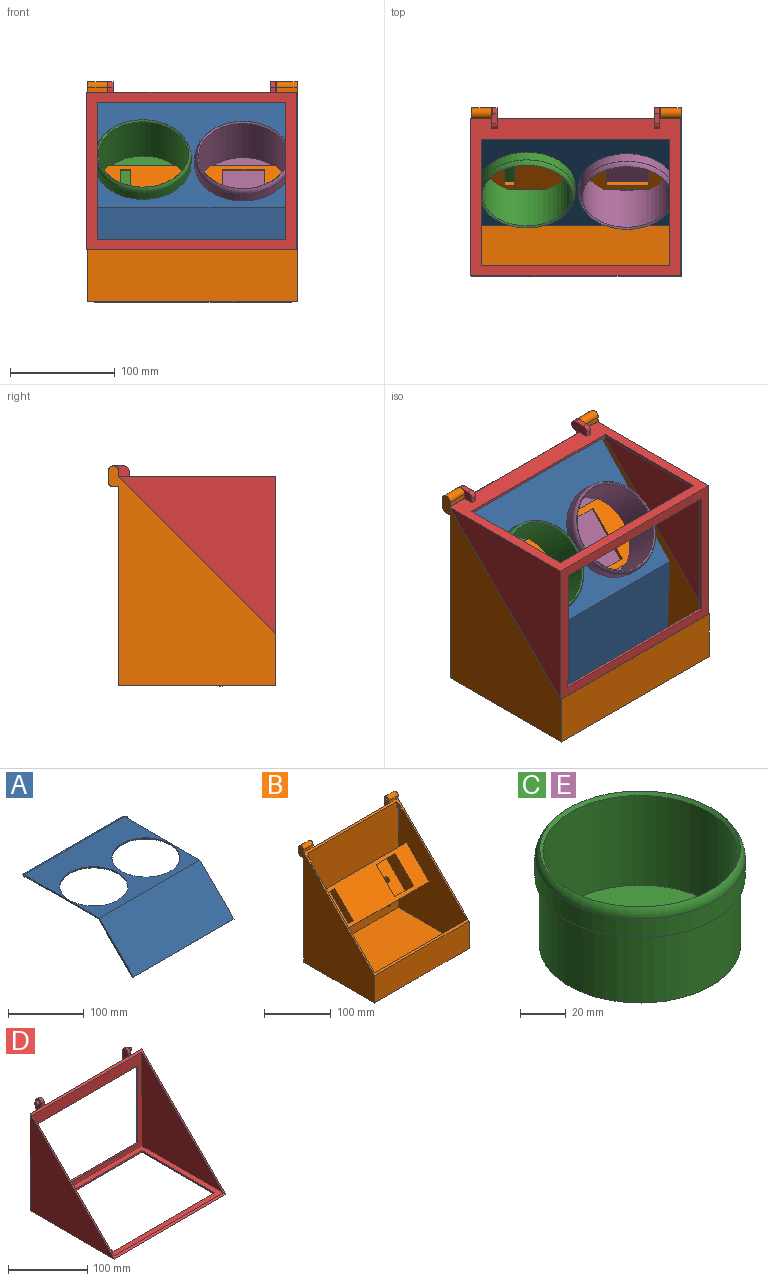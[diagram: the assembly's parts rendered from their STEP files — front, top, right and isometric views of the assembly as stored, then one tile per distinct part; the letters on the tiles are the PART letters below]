
ASSEMBLY  parts=5 mates=4
PART A: 18 faces, bbox 192x208.6x65.6 mm
  f0: plane 4.88x2mm, normal (-1,0,0), area 6.8mm2, adj f4,f5,f8,f13
  f1: plane 4.88x2mm, normal (1,0,0), area 6.8mm2, adj f4,f5,f8,f10
  f2: plane 201.52x65.64mm, normal (-1,0,0), area 527.8mm2, adj f4,f5,f12,f15,f16,f17
  f3: plane 201.52x65.64mm, normal (1,0,0), area 527.8mm2, adj f4,f5,f9,f15,f16,f17
  f4: plane 192x141mm, normal (0,0,1), area 13793.5mm2, adj f0,f1,f2,f3,f6,f7,f8,f9
  f5: plane 192x143mm, normal (0,0,-1), area 14169.5mm2, adj f0,f1,f2,f3,f6,f7,f8,f9
  f6: cylinder r=45mm len=90mm, axis (0,0,1), area 565.5mm2, adj f4,f5
  f7: cylinder r=45mm len=90mm, axis (0,0,1), area 565.5mm2, adj f4,f5
  f8: cylinder r=5mm len=188mm, axis (1,0,0), area 871.7mm2, adj f0,f1,f4,f5
  f9: cylinder r=1.5mm len=2mm, axis (-1,0,0), area 4.4mm2, adj f3,f4,f5,f11
  f10: cylinder r=1.5mm len=2mm, axis (-1,0,0), area 4.4mm2, adj f1,f4,f5,f11
  f11: plane 3x2mm, normal (1,0,0), area 5.5mm2, adj f4,f5,f9,f10
  f12: cylinder r=1.5mm len=2mm, axis (1,0,0), area 4.4mm2, adj f2,f4,f5,f14
  f13: cylinder r=1.5mm len=2mm, axis (1,0,0), area 4.4mm2, adj f0,f4,f5,f14
  f14: plane 3x2mm, normal (-1,0,0), area 5.5mm2, adj f4,f5,f12,f13
  f15: plane 188x63.64mm, normal (0,0.71,-0.71), area 16920mm2, adj f2,f3,f5,f17
  f16: plane 188x63.64mm, normal (0,-0.71,0.71), area 16920mm2, adj f2,f3,f4,f17
  f17: plane 188x2mm, normal (0,-0.71,-0.71), area 531.7mm2, adj f2,f3,f15,f16
PART B: 60 faces, bbox 200x160x210 mm
  f0: plane 19.69x19.58mm, normal (0,-0.71,0.71), area 238.4mm2, adj f43,f44,f45,f56
  f1: plane 185x145mm, normal (-1,0,0), area 14879.1mm2, adj f2,f4,f5,f11,f12,f32,f42,f49
  f2: plane 195x84.64mm, normal (0,-1,0), area 16445.5mm2, adj f1,f3,f4,f30,f31,f32,f33,f49
  f3: plane 185x145mm, normal (1,0,0), area 14879.1mm2, adj f2,f4,f5,f11,f12,f30,f42,f49
  f4: plane 200x150mm, normal (0,-0.71,0.71), area 2495.2mm2, adj f1,f2,f3,f6,f7,f8,f9,f11
  f5: plane 195x62.42mm, normal (0,-1,0), area 12093.3mm2, adj f1,f3,f12,f29,f42
  f6: plane 200x200mm, normal (0,1,0), area 39521.5mm2, adj f4,f7,f9,f10,f13,f14,f16,f17
  f7: plane 210x160mm, normal (-1,0,0), area 18933.9mm2, adj f4,f6,f8,f10,f16,f18,f20,f26
  f8: plane 200x50mm, normal (0,-1,0), area 10000mm2, adj f4,f7,f9,f10
  f9: plane 210x160mm, normal (1,0,0), area 18933.9mm2, adj f4,f6,f8,f10,f13,f15,f19,f25
  f10: plane 200x150mm, normal (0,0,-1), area 30000mm2, adj f6,f7,f8,f9
  f11: plane 195x50mm, normal (0,1,0), area 9750mm2, adj f1,f3,f4,f12
  f12: plane 195x145mm, normal (0,0,1), area 28275mm2, adj f1,f3,f5,f11
  f13: plane 20x5mm, normal (0,0,-1), area 100mm2, adj f6,f9,f14,f28
  f14: plane 20x10mm, normal (-1,0,0), area 164.3mm2, adj f6,f13,f15,f19,f22,f25,f28
  f15: plane 20x10mm, normal (0,1,0), area 200mm2, adj f9,f14,f25,f28
  f16: plane 20x5mm, normal (0,0,-1), area 100mm2, adj f6,f7,f17,f27
  f17: plane 20x10mm, normal (1,0,0), area 164.3mm2, adj f6,f16,f18,f20,f24,f26,f27
  f18: plane 20x10mm, normal (0,1,0), area 200mm2, adj f7,f17,f26,f27
  f19: plane 20x5mm, normal (0,-1,0), area 100mm2, adj f4,f9,f14,f25
  f20: plane 20x5mm, normal (0,-1,0), area 100mm2, adj f4,f7,f17,f26
  f21: cone r=0mm half-angle=59deg, axis (-1,0,0), area 22.9mm2, adj f22
  f22: cylinder r=2.5mm len=5mm, axis (-1,0,0), area 78.5mm2, adj f14,f21
  f23: cone r=0mm half-angle=59deg, axis (1,0,0), area 22.9mm2, adj f24
  f24: cylinder r=2.5mm len=5mm, axis (1,0,0), area 78.5mm2, adj f17,f23
  f25: cylinder r=5mm len=20mm, axis (1,0,0), area 314.2mm2, adj f9,f14,f15,f19
  f26: cylinder r=5mm len=20mm, axis (1,0,0), area 314.2mm2, adj f7,f17,f18,f20
  f27: cylinder r=5mm len=20mm, axis (1,0,0), area 157.1mm2, adj f7,f16,f17,f18
  f28: cylinder r=5mm len=20mm, axis (1,0,0), area 157.1mm2, adj f9,f13,f14,f15
  f29: cylinder r=5mm len=10mm, axis (0,1,0), area 78.5mm2, adj f5,f6
  f30: plane 10x3mm, normal (0,0,-1), area 30mm2, adj f2,f3,f4,f31
  f31: plane 10x10mm, normal (1,0,0), area 30mm2, adj f2,f4,f30,f34,f35,f36
  f32: plane 10x3mm, normal (0,0,-1), area 30mm2, adj f1,f2,f4,f33
  f33: plane 10x10mm, normal (-1,0,0), area 31.2mm2, adj f2,f4,f32,f38,f39,f40
  f34: plane 4.94x2mm, normal (0,0,1), area 9.9mm2, adj f31,f35,f36,f37
  f35: plane 6.74x2mm, normal (0,-1,0.08), area 13.5mm2, adj f4,f31,f34,f37
  f36: plane 2x1.42mm, normal (0,0.99,-0.12), area 2.9mm2, adj f4,f31,f34,f37
  f37: plane 6.74x5.49mm, normal (1,0,0), area 20mm2, adj f4,f34,f35,f36
  f38: plane 5x2mm, normal (0,0,1), area 10mm2, adj f33,f39,f40,f41
  f39: plane 2x1.25mm, normal (0,1,0), area 2.5mm2, adj f4,f33,f38,f41
  f40: plane 6.25x2mm, normal (0,-1,0), area 12.5mm2, adj f4,f33,f38,f41
  f41: plane 6.25x5mm, normal (-1,0,0), area 18.8mm2, adj f4,f38,f39,f40
  f42: plane 195x47.69mm, normal (0,0,-1), area 9298.8mm2, adj f1,f3,f5,f50
  f43: plane 57x56.89mm, normal (1,0,0), area 1388.3mm2, adj f0,f44,f52,f53,f55
  f44: plane 17.72x17.63mm, normal (0,-0.71,-0.71), area 250mm2, adj f0,f43,f45,f53
  f45: plane 57x56.89mm, normal (-1,0,0), area 1388.3mm2, adj f0,f44,f52,f53,f55
  f46: plane 40x17.72mm, normal (0,0.71,0.71), area 1000mm2, adj f47,f51,f53,f54
  f47: plane 57x56.89mm, normal (1,0,0), area 1388.3mm2, adj f46,f48,f53,f54
  f48: plane 40x17.72mm, normal (0,-0.71,-0.71), area 1000mm2, adj f47,f51,f53,f54
  f49: plane 195x17.72mm, normal (0,0.71,0.71), area 4875mm2, adj f1,f2,f3,f53
  f50: plane 195x17.72mm, normal (0,-0.71,-0.71), area 4875mm2, adj f1,f3,f42,f53
  f51: plane 57x56.89mm, normal (-1,0,0), area 1388.3mm2, adj f46,f48,f53,f54
  f52: plane 17.72x17.63mm, normal (0,0.71,0.71), area 250mm2, adj f43,f45,f53,f55
  f53: plane 195x47.94mm, normal (0,-0.71,0.71), area 10408.5mm2, adj f1,f3,f43,f44,f45,f46,f47,f48
  f54: plane 40x39.37mm, normal (0,-0.71,0.71), area 2142.8mm2, adj f46,f47,f48,f51,f58
  f55: plane 19.69x19.58mm, normal (0,-0.71,0.71), area 238.4mm2, adj f43,f45,f52,f56
  f56: cylinder r=5mm len=24.78mm, axis (0,-0.71,0.71), area 785.4mm2, adj f0,f55,f57
  f57: plane 10x7.09mm, normal (0,-0.71,0.71), area 78.5mm2, adj f56
  f58: cylinder r=5mm len=24.78mm, axis (0,-0.71,0.71), area 785.4mm2, adj f54,f59
  f59: plane 10x7.09mm, normal (0,-0.71,0.71), area 78.5mm2, adj f58
PART C: 8 faces, bbox 99.6x99.6x53.4 mm
  f0: cone r=42.5mm half-angle=44.4deg, axis (0,0,1), area 542.9mm2, adj f1,f3
  f1: torus R=39mm, axis (0,0,1), area 1584.2mm2, adj f0,f4
  f2: plane 85x85mm, normal (0,0,1), area 5674.5mm2, adj f3
  f3: cylinder r=42.5mm len=85mm, axis (0,0,1), area 12817.7mm2, adj f0,f2
  f4: cylinder r=46mm len=92mm, axis (0,0,1), area 2890.3mm2, adj f1,f5
  f5: plane 92x92mm, normal (0,0,-1), area 565.5mm2, adj f4,f7
  f6: plane 88x88mm, normal (0,0,-1), area 6082.1mm2, adj f7
  f7: cylinder r=44mm len=88mm, axis (0,0,-1), area 10071.2mm2, adj f5,f6
PART D: 35 faces, bbox 200x160x160 mm
  f0: plane 200x150mm, normal (0,0,-1), area 6600mm2, adj f2,f4,f5,f6,f31,f32,f33,f34
  f1: plane 195x145mm, normal (0,0,1), area 4875mm2, adj f3,f4,f7,f8,f31,f32,f33,f34
  f2: plane 200x150mm, normal (0,1,0), area 8300mm2, adj f0,f4,f5,f6,f9,f10,f11,f13
  f3: plane 195x145mm, normal (0,-1,0), area 6675mm2, adj f1,f4,f7,f8,f27,f28,f29,f30
  f4: plane 200x150mm, normal (0,-0.71,0.71), area 2439.5mm2, adj f0,f1,f2,f3,f5,f6,f7,f8
  f5: plane 150x150mm, normal (-1,0,0), area 11250mm2, adj f0,f2,f4
  f6: plane 150x150mm, normal (1,0,0), area 11250mm2, adj f0,f2,f4
  f7: plane 145x145mm, normal (1,0,0), area 10512.5mm2, adj f1,f3,f4
  f8: plane 145x145mm, normal (-1,0,0), area 10512.5mm2, adj f1,f3,f4
  f9: plane 20x10mm, normal (1,0,0), area 171.3mm2, adj f2,f10,f12,f17,f19,f24,f26
  f10: plane 5x5mm, normal (0,0,-1), area 25mm2, adj f2,f9,f11,f26
  f11: plane 20x10mm, normal (-1,0,0), area 183.9mm2, adj f2,f10,f12,f17,f24,f26
  f12: plane 10x5mm, normal (0,1,0), area 50mm2, adj f9,f11,f24,f26
  f13: plane 20x10mm, normal (-1,0,0), area 164.3mm2, adj f2,f15,f16,f18,f21,f23,f25
  f14: plane 20x10mm, normal (1,0,0), area 183.9mm2, adj f2,f15,f16,f18,f23,f25
  f15: plane 5x5mm, normal (0,0,-1), area 25mm2, adj f2,f13,f14,f25
  f16: plane 10x5mm, normal (0,1,0), area 50mm2, adj f13,f14,f23,f25
  f17: plane 5x5mm, normal (0,-1,0), area 25mm2, adj f4,f9,f11,f24
  f18: plane 5x5mm, normal (0,-1,0), area 25mm2, adj f4,f13,f14,f23
  f19: cylinder r=2mm len=5mm, axis (-1,0,0), area 62.8mm2, adj f9,f20
  f20: plane 4x4mm, normal (1,0,0), area 12.6mm2, adj f19
  f21: cylinder r=2.5mm len=5mm, axis (1,0,0), area 78.5mm2, adj f13,f22
  f22: plane 5x5mm, normal (-1,0,0), area 19.6mm2, adj f21
  f23: cylinder r=5mm len=10mm, axis (1,0,0), area 78.5mm2, adj f13,f14,f16,f18
  f24: cylinder r=5mm len=10mm, axis (1,0,0), area 78.5mm2, adj f9,f11,f12,f17
  f25: cylinder r=5mm len=5mm, axis (1,0,0), area 39.3mm2, adj f13,f14,f15,f16
  f26: cylinder r=5mm len=5mm, axis (1,0,0), area 39.3mm2, adj f9,f10,f11,f12
  f27: plane 180x2.5mm, normal (0,0,-1), area 450mm2, adj f2,f3,f28,f30
  f28: plane 120x2.5mm, normal (-1,0,0), area 300mm2, adj f2,f3,f27,f29
  f29: plane 180x2.5mm, normal (0,0,1), area 450mm2, adj f2,f3,f28,f30
  f30: plane 120x2.5mm, normal (1,0,0), area 300mm2, adj f2,f3,f27,f29
  f31: plane 180x2.5mm, normal (0,1,0), area 450mm2, adj f0,f1,f32,f34
  f32: plane 130x2.5mm, normal (1,0,0), area 325mm2, adj f0,f1,f31,f33
  f33: plane 180x2.5mm, normal (0,-1,0), area 450mm2, adj f0,f1,f32,f34
  f34: plane 130x2.5mm, normal (-1,0,0), area 325mm2, adj f0,f1,f31,f33
PART E: same geometry as C
PLACE A rot(axis=(1,0,0),47.1deg) t=(-7.12,554.89,88.45)mm
PLACE B t=(-5.43,539.67,-44.03)mm fixed
PLACE C rot(axis=(0.7,-0.29,0.66),64deg) t=(-52.68,577.93,62.66)mm
PLACE D rot(axis=(0,-0.71,-0.71),180deg) t=(-6.18,464.7,80.91)mm
PLACE E rot(axis=(0.14,-0.4,0.91),143.5deg) t=(42.82,576.57,61.19)mm
MATE revolute A.f9 <-> B.f41  axis (1,0,0) through (91.07,607.72,146.87)mm
MATE revolute D.f19 <-> B.f21  axis (-1,0,0) through (-91.18,619.67,160.97)mm
MATE revolute E.f0 <-> A.f6  axis (0,0.73,-0.68) through (42.82,549.86,85.97)mm
MATE revolute C.f0 <-> A.f7  axis (0,0.73,-0.68) through (-52.68,551.22,87.43)mm
